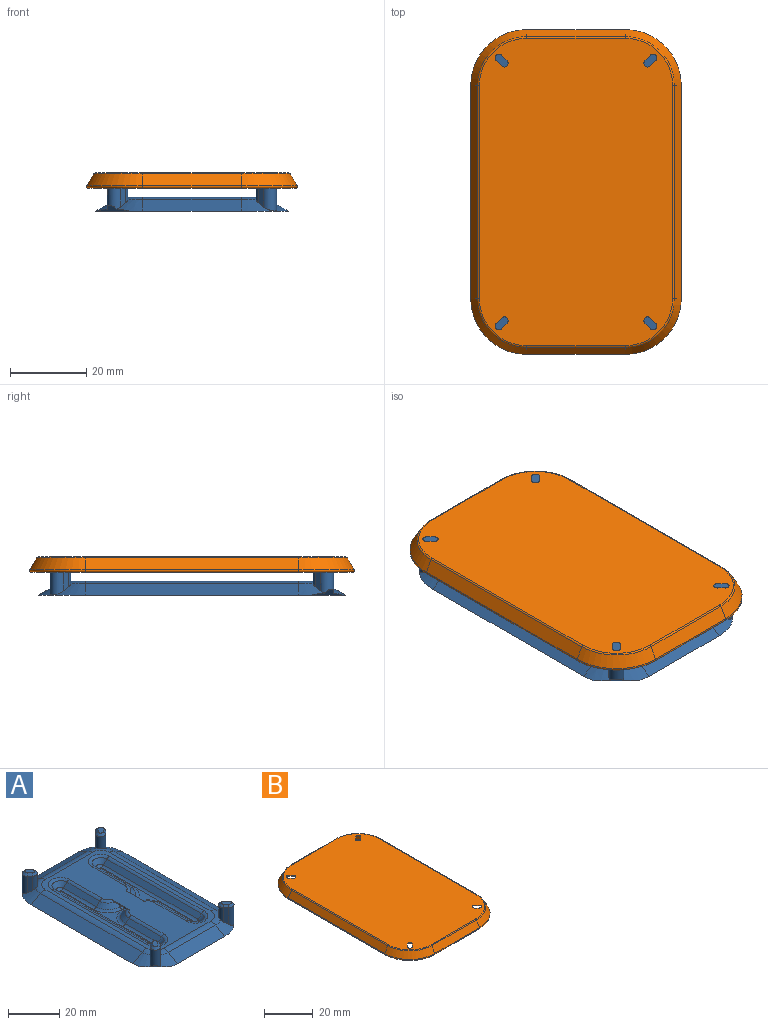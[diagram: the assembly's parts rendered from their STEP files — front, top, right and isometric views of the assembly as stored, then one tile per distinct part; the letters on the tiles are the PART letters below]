
ASSEMBLY  parts=2 mates=1
PART A: 109 faces, bbox 50.6x80.6x10.1 mm
  f0: cone r=6mm half-angle=60deg, axis (0,0,-1), area 30.9mm2, adj f2,f14,f15,f98,f99,f105,f108
  f1: cone r=6mm half-angle=60deg, axis (0,0,-1), area 30.9mm2, adj f2,f15,f71,f97,f98,f105,f108
  f2: cylinder r=2mm len=8.5mm, axis (0,0,-1), area 50.1mm2, adj f0,f1,f97,f99,f101,f108
  f3: cone r=6mm half-angle=60deg, axis (0,0,-1), area 33.9mm2, adj f14,f15,f52,f53,f54,f61
  f4: cone r=6mm half-angle=60deg, axis (0,0,-1), area 33.9mm2, adj f13,f15,f39,f40,f42,f64
  f5: cone r=6mm half-angle=60deg, axis (0,0,-1), area 33.9mm2, adj f13,f15,f51,f52,f54,f61
  f6: cone r=4mm half-angle=45deg, axis (0,0,-1), area 22.3mm2, adj f7,f21,f28,f35,f48,f50
  f7: plane 6x1.81mm, normal (0,-0.71,0.71), area 15.4mm2, adj f6,f8,f27,f48
  f8: cone r=4mm half-angle=45deg, axis (0,0,-1), area 22.3mm2, adj f7,f9,f16,f26,f48,f49
  f9: torus R=3.17mm, axis (0,0,1), area 8mm2, adj f8,f10,f34,f49
  f10: plane 65.32x35.32mm, normal (0,0,1), area 1087.4mm2, adj f9,f32,f33,f34,f35,f36,f37,f38
  f11: plane 56x5.08mm, normal (0.5,0,0.87), area 328.2mm2, adj f12,f15,f62,f70
  f12: cone r=6mm half-angle=60deg, axis (0,0,-1), area 33.9mm2, adj f11,f15,f40,f41,f42,f64
  f13: plane 26x5.08mm, normal (0,0.5,0.87), area 152.4mm2, adj f4,f5,f15,f63
  f14: plane 56x5.08mm, normal (-0.5,0,0.87), area 328.2mm2, adj f0,f3,f15,f60
  f15: plane 80.47x50.47mm, normal (0,0,-1), area 3921mm2, adj f0,f1,f3,f4,f5,f11,f12,f13
  f16: plane 18x1.83mm, normal (-0.71,0,0.71), area 46.5mm2, adj f8,f17,f25,f34
  f17: cone r=4mm half-angle=45deg, axis (0,0,1), area 20.3mm2, adj f16,f18,f24,f33
  f18: plane 52x1.83mm, normal (0.71,0,0.71), area 134.5mm2, adj f17,f23,f32,f73
  f19: plane 52x1.83mm, normal (-0.71,0,0.71), area 134.5mm2, adj f20,f30,f38,f74
  f20: cone r=4mm half-angle=45deg, axis (0,0,1), area 20.3mm2, adj f19,f21,f31,f37
  f21: plane 18x1.83mm, normal (0.71,0,0.71), area 46.5mm2, adj f6,f20,f29,f36
  f22: plane 52.34x22.34mm, normal (0,0,1), area 95.9mm2, adj f23,f24,f25,f26,f27,f28,f29,f30
  f23: cylinder r=2mm len=52mm, axis (0,-1,0), area 81.7mm2, adj f18,f22,f24,f76
  f24: torus R=0.17mm, axis (0,0,1), area 4.5mm2, adj f17,f22,f23,f25
  f25: cylinder r=2mm len=18mm, axis (0,1,0), area 28.3mm2, adj f16,f22,f24,f26
  f26: torus R=7.83mm, axis (0,0,1), area 17.5mm2, adj f8,f22,f25,f27
  f27: cylinder r=2mm len=6mm, axis (-1,0,0), area 9.4mm2, adj f7,f22,f26,f28
  f28: torus R=7.83mm, axis (0,0,1), area 17.5mm2, adj f6,f22,f27,f29
  f29: cylinder r=2mm len=18mm, axis (0,-1,0), area 28.3mm2, adj f21,f22,f28,f31
  f30: cylinder r=2mm len=52mm, axis (0,1,0), area 81.7mm2, adj f19,f22,f31,f82
  f31: torus R=0.17mm, axis (0,0,1), area 4.5mm2, adj f20,f22,f29,f30
  f32: cylinder r=2mm len=52mm, axis (0,-1,0), area 81.7mm2, adj f10,f18,f33,f83
  f33: torus R=4.83mm, axis (0,0,1), area 20.1mm2, adj f10,f17,f32,f34
  f34: cylinder r=2mm len=18mm, axis (0,1,0), area 28.3mm2, adj f9,f10,f16,f33
  f35: torus R=3.17mm, axis (0,0,1), area 8mm2, adj f6,f10,f36,f50
  f36: cylinder r=2mm len=18mm, axis (0,-1,0), area 28.3mm2, adj f10,f21,f35,f37
  f37: torus R=4.83mm, axis (0,0,1), area 20.1mm2, adj f10,f20,f36,f38
  f38: cylinder r=2mm len=52mm, axis (0,1,0), area 81.7mm2, adj f10,f19,f37,f87
  f39: plane 8x1.46mm, normal (-0.71,0.71,0), area 14.8mm2, adj f4,f40,f42,f46
  f40: cylinder r=2mm len=9mm, axis (0,0,-1), area 54.2mm2, adj f4,f12,f39,f41,f44
  f41: plane 8x1.46mm, normal (0.71,-0.71,0), area 14.8mm2, adj f12,f40,f42,f45
  f42: cylinder r=2mm len=6.83mm, axis (0,0,-1), area 38.1mm2, adj f4,f12,f39,f41,f47,f64
  f43: plane 3.41x3.41mm, normal (0,0,1), area 7.1mm2, adj f44,f45,f46,f47
  f44: cone r=2mm half-angle=45deg, axis (0,0,-1), area 6.7mm2, adj f40,f43,f45,f46
  f45: plane 2.12x2.12mm, normal (0.5,-0.5,0.71), area 2.8mm2, adj f41,f43,f44,f47
  f46: plane 2.12x2.12mm, normal (-0.5,0.5,0.71), area 2.8mm2, adj f39,f43,f44,f47
  f47: cone r=2mm half-angle=45deg, axis (0,0,-1), area 6.7mm2, adj f42,f43,f45,f46
  f48: plane 8x7.02mm, normal (0,0,-1), area 54.5mm2, adj f6,f7,f8,f49,f50,f66,f67,f68
  f49: plane 10.09x0.7mm, normal (-1,0,0), area 4.8mm2, adj f8,f9,f10,f48,f68,f69
  f50: plane 10.09x0.7mm, normal (1,0,0), area 4.8mm2, adj f6,f10,f35,f48,f66,f85
  f51: plane 8x1.46mm, normal (0.71,0.71,0), area 14.8mm2, adj f5,f52,f54,f58
  f52: cylinder r=2mm len=6.83mm, axis (0,0,-1), area 38.1mm2, adj f3,f5,f51,f53,f59,f61
  f53: plane 8x1.46mm, normal (-0.71,-0.71,0), area 14.8mm2, adj f3,f52,f54,f57
  f54: cylinder r=2mm len=9mm, axis (0,0,-1), area 54.2mm2, adj f3,f5,f51,f53,f56
  f55: plane 3.41x3.41mm, normal (0,0,1), area 7.1mm2, adj f56,f57,f58,f59
  f56: cone r=1mm half-angle=45deg, axis (0,0,-1), area 6.7mm2, adj f54,f55,f57,f58
  f57: plane 2.12x2.12mm, normal (-0.5,-0.5,0.71), area 2.8mm2, adj f53,f55,f56,f59
  f58: plane 2.12x2.12mm, normal (0.5,0.5,0.71), area 2.8mm2, adj f51,f55,f56,f59
  f59: cone r=1mm half-angle=45deg, axis (0,0,-1), area 6.7mm2, adj f52,f55,f57,f58
  f60: cylinder r=5mm len=56mm, axis (0,1,0), area 146.6mm2, adj f10,f14,f61,f105
  f61: torus R=4.66mm, axis (0,0,1), area 22.2mm2, adj f3,f5,f10,f52,f60,f63
  f62: cylinder r=5mm len=56mm, axis (0,1,0), area 146.6mm2, adj f10,f11,f64,f107
  f63: cylinder r=5mm len=26mm, axis (1,0,0), area 68.1mm2, adj f10,f13,f61,f64
  f64: torus R=4.66mm, axis (0,0,1), area 22.2mm2, adj f4,f10,f12,f42,f62,f63
  f65: cone r=6mm half-angle=60deg, axis (0,0,-1), area 33.9mm2, adj f15,f71,f88,f89,f91,f107
  f66: cone r=4mm half-angle=45deg, axis (0,0,-1), area 22.3mm2, adj f48,f50,f67,f75,f80,f85
  f67: plane 6x1.81mm, normal (0,0.71,0.71), area 15.4mm2, adj f48,f66,f68,f79
  f68: cone r=4mm half-angle=45deg, axis (0,0,-1), area 22.3mm2, adj f48,f49,f67,f69,f72,f78
  f69: torus R=3.17mm, axis (0,0,1), area 8mm2, adj f10,f49,f68,f84
  f70: cone r=6mm half-angle=60deg, axis (0,0,-1), area 33.9mm2, adj f11,f15,f89,f90,f91,f107
  f71: plane 26x5.08mm, normal (0,-0.5,0.87), area 152.4mm2, adj f1,f15,f65,f106
  f72: plane 18x1.83mm, normal (-0.71,0,0.71), area 46.5mm2, adj f68,f73,f77,f84
  f73: cone r=4mm half-angle=45deg, axis (0,0,1), area 20.3mm2, adj f18,f72,f76,f83
  f74: cone r=4mm half-angle=45deg, axis (0,0,1), area 20.3mm2, adj f19,f75,f82,f87
  f75: plane 18x1.83mm, normal (0.71,0,0.71), area 46.5mm2, adj f66,f74,f81,f86
  f76: torus R=0.17mm, axis (0,0,1), area 4.5mm2, adj f22,f23,f73,f77
  f77: cylinder r=2mm len=18mm, axis (0,-1,0), area 28.3mm2, adj f22,f72,f76,f78
  f78: torus R=7.83mm, axis (0,0,1), area 17.5mm2, adj f22,f68,f77,f79
  f79: cylinder r=2mm len=6mm, axis (-1,0,0), area 9.4mm2, adj f22,f67,f78,f80
  f80: torus R=7.83mm, axis (0,0,1), area 17.5mm2, adj f22,f66,f79,f81
  f81: cylinder r=2mm len=18mm, axis (0,1,0), area 28.3mm2, adj f22,f75,f80,f82
  f82: torus R=0.17mm, axis (0,0,1), area 4.5mm2, adj f22,f30,f74,f81
  f83: torus R=4.83mm, axis (0,0,1), area 20.1mm2, adj f10,f32,f73,f84
  f84: cylinder r=2mm len=18mm, axis (0,-1,0), area 28.3mm2, adj f10,f69,f72,f83
  f85: torus R=3.17mm, axis (0,0,1), area 8mm2, adj f10,f50,f66,f86
  f86: cylinder r=2mm len=18mm, axis (0,1,0), area 28.3mm2, adj f10,f75,f85,f87
  f87: torus R=4.83mm, axis (0,0,1), area 20.1mm2, adj f10,f38,f74,f86
  f88: plane 8x1.46mm, normal (-0.71,-0.71,0), area 14.8mm2, adj f65,f89,f91,f95
  f89: cylinder r=2mm len=9mm, axis (0,0,-1), area 54.2mm2, adj f65,f70,f88,f90,f93
  f90: plane 8x1.46mm, normal (0.71,0.71,0), area 14.8mm2, adj f70,f89,f91,f94
  f91: cylinder r=2mm len=6.83mm, axis (0,0,-1), area 38.1mm2, adj f65,f70,f88,f90,f96,f107
  f92: plane 3.41x3.41mm, normal (0,0,1), area 7.1mm2, adj f93,f94,f95,f96
  f93: cone r=2mm half-angle=45deg, axis (0,0,-1), area 6.7mm2, adj f89,f92,f94,f95
  f94: plane 2.12x2.12mm, normal (0.5,0.5,0.71), area 2.8mm2, adj f90,f92,f93,f96
  f95: plane 2.12x2.12mm, normal (-0.5,-0.5,0.71), area 2.8mm2, adj f88,f92,f93,f96
  f96: cone r=2mm half-angle=45deg, axis (0,0,-1), area 6.7mm2, adj f91,f92,f94,f95
  f97: plane 8x1.46mm, normal (0.71,-0.71,0), area 14.8mm2, adj f1,f2,f98,f103
  f98: cylinder r=2mm len=6.83mm, axis (0,0,-1), area 38.1mm2, adj f0,f1,f97,f99,f104,f105
  f99: plane 8x1.46mm, normal (-0.71,0.71,0), area 14.8mm2, adj f0,f2,f98,f102
  f100: plane 3.41x3.41mm, normal (0,0,1), area 7.1mm2, adj f101,f102,f103,f104
  f101: cone r=1mm half-angle=45deg, axis (0,0,-1), area 6.7mm2, adj f2,f100,f102,f103
  f102: plane 2.12x2.12mm, normal (-0.5,0.5,0.71), area 2.8mm2, adj f99,f100,f101,f104
  f103: plane 2.12x2.12mm, normal (0.5,-0.5,0.71), area 2.8mm2, adj f97,f100,f101,f104
  f104: cone r=1mm half-angle=45deg, axis (0,0,-1), area 6.7mm2, adj f98,f100,f102,f103
  f105: torus R=4.66mm, axis (0,0,1), area 22.2mm2, adj f0,f1,f10,f60,f98,f106
  f106: cylinder r=5mm len=26mm, axis (1,0,0), area 68.1mm2, adj f10,f71,f105,f107
  f107: torus R=4.66mm, axis (0,0,1), area 22.2mm2, adj f10,f62,f65,f70,f91,f106
  f108: plane 8.3x8.3mm, normal (-0.5,-0.5,-0.71), area 9.4mm2, adj f0,f1,f2,f15
PART B: 83 faces, bbox 57.7x87.7x4 mm
  f0: plane 80.74x50.74mm, normal (0,0,1), area 3936.7mm2, adj f2,f3,f4,f5,f6,f7,f8,f9
  f1: plane 80.47x50.47mm, normal (0,0,-1), area 1043.7mm2, adj f2,f3,f4,f5,f6,f7,f8,f9
  f2: cone r=2mm half-angle=45deg, axis (0,0,-1), area 6.7mm2, adj f0,f1,f3,f4
  f3: plane 2.12x2.12mm, normal (-0.5,-0.5,-0.71), area 2.8mm2, adj f0,f1,f2,f5
  f4: plane 2.12x2.12mm, normal (0.5,0.5,-0.71), area 2.8mm2, adj f0,f1,f2,f5
  f5: cone r=2mm half-angle=45deg, axis (0,0,-1), area 6.7mm2, adj f0,f1,f3,f4
  f6: cone r=1mm half-angle=45deg, axis (0,0,-1), area 6.7mm2, adj f0,f1,f7,f8
  f7: plane 2.12x2.12mm, normal (-0.5,0.5,-0.71), area 2.8mm2, adj f0,f1,f6,f9
  f8: plane 2.12x2.12mm, normal (0.5,-0.5,-0.71), area 2.8mm2, adj f0,f1,f6,f9
  f9: cone r=1mm half-angle=45deg, axis (0,0,-1), area 6.7mm2, adj f0,f1,f7,f8
  f10: cone r=1mm half-angle=45deg, axis (0,0,-1), area 6.7mm2, adj f0,f1,f11,f12
  f11: plane 2.12x2.12mm, normal (0.5,-0.5,-0.71), area 2.8mm2, adj f0,f1,f10,f13
  f12: plane 2.12x2.12mm, normal (-0.5,0.5,-0.71), area 2.8mm2, adj f0,f1,f10,f13
  f13: cone r=1mm half-angle=45deg, axis (0,0,-1), area 6.7mm2, adj f0,f1,f11,f12
  f14: cone r=2mm half-angle=45deg, axis (0,0,-1), area 6.7mm2, adj f0,f1,f15,f16
  f15: plane 2.12x2.12mm, normal (0.5,0.5,-0.71), area 2.8mm2, adj f0,f1,f14,f17
  f16: plane 2.12x2.12mm, normal (-0.5,-0.5,-0.71), area 2.8mm2, adj f0,f1,f14,f17
  f17: cone r=2mm half-angle=45deg, axis (0,0,-1), area 6.7mm2, adj f0,f1,f15,f16
  f18: cylinder r=0.43mm len=26mm, axis (1,0,0), area 35.4mm2, adj f19,f20,f23,f47
  f19: plane 26x2.78mm, normal (0,0.87,-0.5), area 83.6mm2, adj f1,f18,f22,f46
  f20: plane 26x3.1mm, normal (0,-0.87,0.5), area 93.1mm2, adj f18,f21,f24,f48
  f21: cylinder r=0.5mm len=26mm, axis (1,0,0), area 13.6mm2, adj f0,f20,f25,f49
  f22: cone r=12.24mm half-angle=30deg, axis (0,0,-1), area 65.8mm2, adj f1,f19,f23,f26
  f23: torus R=14.22mm, axis (0,0,-1), area 30.7mm2, adj f18,f22,f24,f27
  f24: cone r=14.59mm half-angle=30deg, axis (0,0,-1), area 77mm2, adj f20,f23,f25,f28
  f25: torus R=12.37mm, axis (0,0,-1), area 10.4mm2, adj f0,f21,f24,f29
  f26: plane 56x2.78mm, normal (0.87,0,-0.5), area 180mm2, adj f1,f22,f27,f30
  f27: cylinder r=0.43mm len=56mm, axis (0,1,0), area 76.2mm2, adj f23,f26,f28,f31
  f28: plane 56x3.1mm, normal (-0.87,0,0.5), area 200.5mm2, adj f24,f27,f29,f32
  f29: cylinder r=0.5mm len=56mm, axis (0,1,0), area 29.3mm2, adj f0,f25,f28,f33
  f30: cone r=12.24mm half-angle=30deg, axis (0,0,-1), area 65.8mm2, adj f1,f26,f31,f34
  f31: torus R=14.22mm, axis (0,0,-1), area 30.7mm2, adj f27,f30,f32,f35
  f32: cone r=14.59mm half-angle=30deg, axis (0,0,-1), area 77mm2, adj f28,f31,f33,f36
  f33: torus R=12.37mm, axis (0,0,-1), area 10.4mm2, adj f0,f29,f32,f37
  f34: plane 26x2.78mm, normal (0,-0.87,-0.5), area 83.6mm2, adj f1,f30,f35,f38
  f35: cylinder r=0.43mm len=26mm, axis (1,0,0), area 35.4mm2, adj f31,f34,f36,f39
  f36: plane 26x3.1mm, normal (0,0.87,0.5), area 93.1mm2, adj f32,f35,f37,f40
  f37: cylinder r=0.5mm len=26mm, axis (1,0,0), area 13.6mm2, adj f0,f33,f36,f41
  f38: cone r=12.24mm half-angle=30deg, axis (0,0,-1), area 65.8mm2, adj f1,f34,f39,f42
  f39: torus R=14.22mm, axis (0,0,-1), area 30.7mm2, adj f35,f38,f40,f43
  f40: cone r=14.59mm half-angle=30deg, axis (0,0,-1), area 77mm2, adj f36,f39,f41,f44
  f41: torus R=12.37mm, axis (0,0,-1), area 10.4mm2, adj f0,f37,f40,f45
  f42: plane 56x2.78mm, normal (-0.87,0,-0.5), area 180mm2, adj f1,f38,f43,f46
  f43: cylinder r=0.43mm len=56mm, axis (0,-1,0), area 76.2mm2, adj f39,f42,f44,f47
  f44: plane 56x3.1mm, normal (0.87,0,0.5), area 200.5mm2, adj f40,f43,f45,f48
  f45: cylinder r=0.5mm len=56mm, axis (0,-1,0), area 29.3mm2, adj f0,f41,f44,f49
  f46: cone r=12.24mm half-angle=30deg, axis (0,0,-1), area 65.8mm2, adj f1,f19,f42,f47
  f47: torus R=14.22mm, axis (0,0,-1), area 30.7mm2, adj f18,f43,f46,f48
  f48: cone r=14.59mm half-angle=30deg, axis (0,0,-1), area 77mm2, adj f20,f44,f47,f49
  f49: torus R=12.37mm, axis (0,0,-1), area 10.4mm2, adj f0,f21,f45,f48
  f50: plane 5x0.4mm, normal (1,0,0), area 2mm2, adj f1,f51,f81,f82
  f51: cylinder r=3mm len=3mm, axis (0,0,-1), area 1.9mm2, adj f1,f50,f52,f82
  f52: cylinder r=3mm len=3mm, axis (0,0,-1), area 1.9mm2, adj f1,f51,f53,f82
  f53: plane 34x0.4mm, normal (1,0,0), area 13.6mm2, adj f1,f52,f54,f82
  f54: cylinder r=3mm len=3mm, axis (0,0,-1), area 1.9mm2, adj f1,f53,f55,f82
  f55: cylinder r=3mm len=3mm, axis (0,0,-1), area 1.9mm2, adj f1,f54,f56,f82
  f56: plane 5x0.4mm, normal (1,0,0), area 2mm2, adj f1,f55,f57,f82
  f57: cylinder r=4.24mm len=4.24mm, axis (0,0,-1), area 2.7mm2, adj f1,f56,f58,f82
  f58: plane 5x0.4mm, normal (0,-1,0), area 2mm2, adj f1,f57,f59,f82
  f59: cylinder r=3mm len=3mm, axis (0,0,-1), area 1.9mm2, adj f1,f58,f60,f82
  f60: cylinder r=3mm len=3mm, axis (0,0,-1), area 1.9mm2, adj f1,f59,f61,f82
  f61: plane 4x0.4mm, normal (0,-1,0), area 1.6mm2, adj f1,f60,f62,f82
  f62: cylinder r=3mm len=3mm, axis (0,0,-1), area 1.9mm2, adj f1,f61,f63,f82
  f63: cylinder r=3mm len=3mm, axis (0,0,-1), area 1.9mm2, adj f1,f62,f64,f82
  f64: plane 5x0.4mm, normal (0,-1,0), area 2mm2, adj f1,f63,f65,f82
  f65: cylinder r=4.24mm len=4.24mm, axis (0,0,-1), area 2.7mm2, adj f1,f64,f66,f82
  f66: plane 5x0.4mm, normal (-1,0,0), area 2mm2, adj f1,f65,f67,f82
  f67: cylinder r=3mm len=3mm, axis (0,0,-1), area 1.9mm2, adj f1,f66,f68,f82
  f68: cylinder r=3mm len=3mm, axis (0,0,-1), area 1.9mm2, adj f1,f67,f69,f82
  f69: plane 34x0.4mm, normal (-1,0,0), area 13.6mm2, adj f1,f68,f70,f82
  f70: cylinder r=3mm len=3mm, axis (0,0,-1), area 1.9mm2, adj f1,f69,f71,f82
  f71: cylinder r=3mm len=3mm, axis (0,0,-1), area 1.9mm2, adj f1,f70,f72,f82
  f72: plane 5x0.4mm, normal (-1,0,0), area 2mm2, adj f1,f71,f73,f82
  f73: cylinder r=4.24mm len=4.24mm, axis (0,0,-1), area 2.7mm2, adj f1,f72,f74,f82
  f74: plane 5x0.4mm, normal (0,1,0), area 2mm2, adj f1,f73,f75,f82
  f75: cylinder r=3mm len=3mm, axis (0,0,-1), area 1.9mm2, adj f1,f74,f76,f82
  f76: cylinder r=3mm len=3mm, axis (0,0,-1), area 1.9mm2, adj f1,f75,f77,f82
  f77: plane 4x0.4mm, normal (0,1,0), area 1.6mm2, adj f1,f76,f78,f82
  f78: cylinder r=3mm len=3mm, axis (0,0,-1), area 1.9mm2, adj f1,f77,f79,f82
  f79: cylinder r=3mm len=3mm, axis (0,0,-1), area 1.9mm2, adj f1,f78,f80,f82
  f80: plane 5x0.4mm, normal (0,1,0), area 2mm2, adj f1,f79,f81,f82
  f81: cylinder r=4.24mm len=4.24mm, axis (0,0,-1), area 2.7mm2, adj f1,f50,f80,f82
  f82: plane 76.47x46.47mm, normal (0,0,-1), area 2807mm2, adj f50,f51,f52,f53,f54,f55,f56,f57
PLACE A t=(4.88,-1.24,9.38)mm
PLACE B t=(4.88,-1.24,-1.62)mm
MATE fastened B.f6 <-> A.f98  axis (0,0,1) through (1.06,-35.07,15.78)mm
